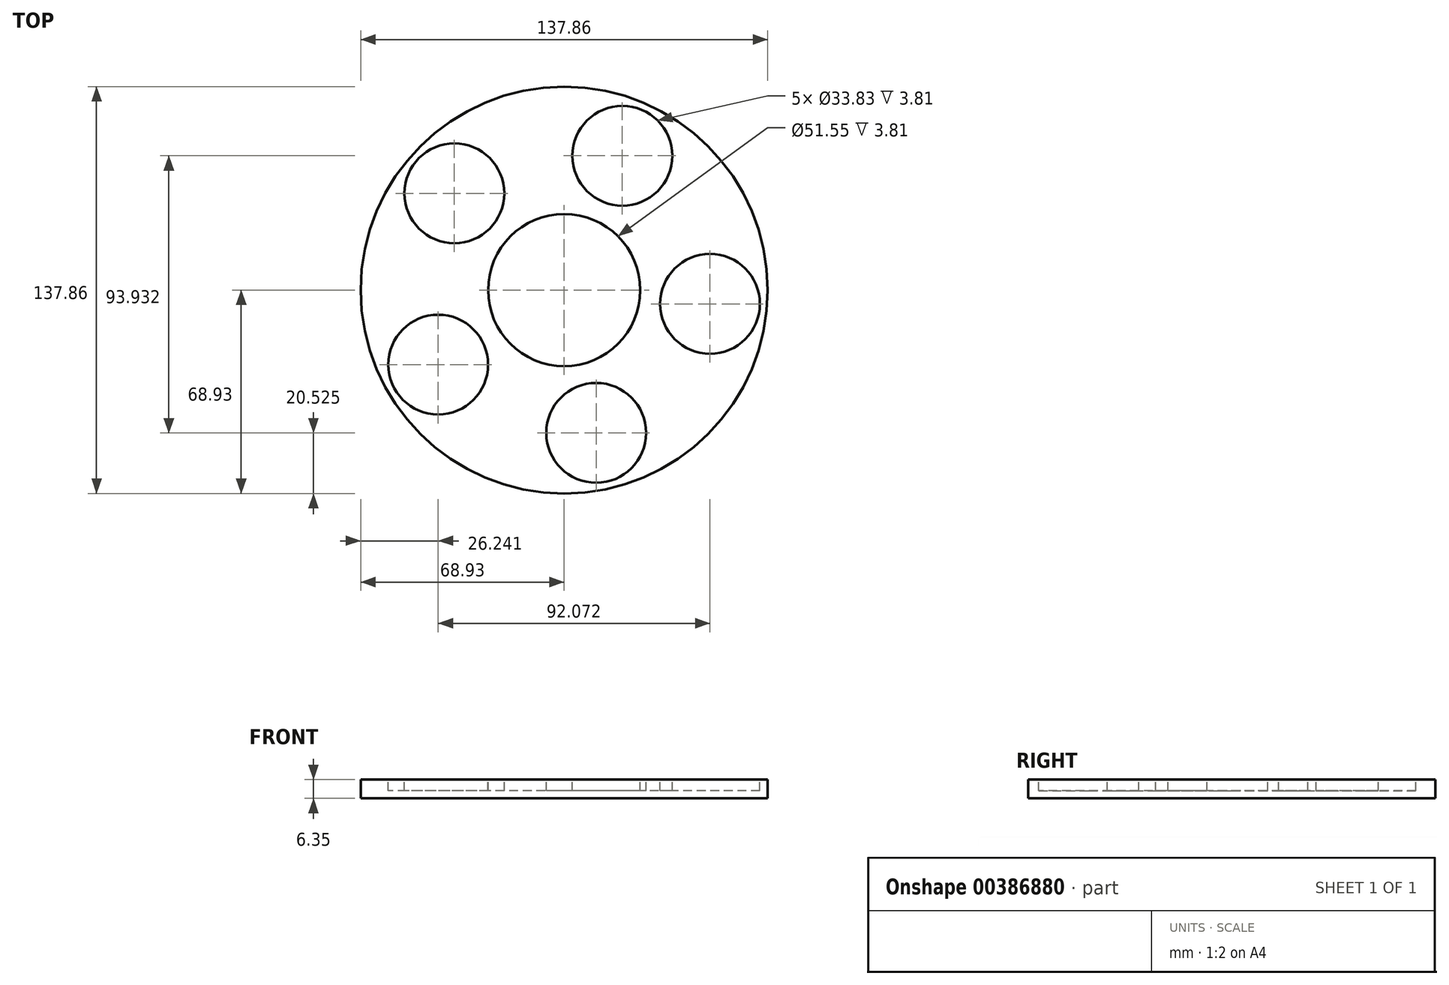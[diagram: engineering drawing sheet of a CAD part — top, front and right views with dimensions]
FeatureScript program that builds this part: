
annotation { "Feature Type Name" : "Feature", "Feature Type Description" : "" }
export const myFeature = defineFeature(function(context is Context, id is Id, definition is map)
    precondition{}
    {
        {
            var Q0;
            Q0=qCreatedBy(makeId("Top.planeOp"),FACE);
            var sketch = newSketch(context, id + "F0", { "sketchPlane" : qUnion([Q0])});
            skCircle(sketch, "E0", {"center": v(0, 0) * mm, "radius": 68.93 * mm});
            skSolve(sketch);
        }
        {
            var Q0;
            Q0 = qSketchRegion(id + "F0", true);
            var Q1;
            Q1 = qSketchRegion(id + "F2", true);
            extrude(context, id + "F1", {"entities" : qUnion([Q0, Q1]), "depth" : 6.35 * mm});
        }
        {
            var Q0;
            Q0=makeQuery(id+"F1.opExtrude","CAP_FACE",FACE,{"disambiguationData":[OSD([sQuery(id+"F0.wireOp",EDGE,"E0")])],"isStart":false});
            var sketch = newSketch(context, id + "F2", { "sketchPlane" : qUnion([Q0])});
            skCircle(sketch, "E1", {"center": v(0, 0) * mm, "radius": 25.78 * mm});
            skSolve(sketch);
        }
        {
            var Q0;
            Q0=makeQuery(id+"F2.imprint","IMPRINT",FACE,{"disambiguationData":[TD([[makeQuery(id+"F2.imprint","IMPRINT",EDGE,{"derivedFrom":sQuery(id+"F2.wireOp",EDGE,"E1")}),1.0]])]});
            extrude(context, id + "F3", {"entities" : qUnion([Q0]), "operationType" : NewBodyOperationType.REMOVE, "oppositeDirection" : true, "depth" : 3.8 * mm});
        }
        {
            var Q0;
            Q0=makeQuery(id+"F1.opExtrude","CAP_FACE",FACE,{"disambiguationData":[OSD([sQuery(id+"F0.wireOp",EDGE,"E0")])],"isStart":false});
            var sketch = newSketch(context, id + "F4", { "sketchPlane" : qUnion([Q0])});
            skSolve(sketch);
        }
        {
            var Q0;
            Q0=makeQuery(id+"F4.imprint","IMPRINT",FACE,{"disambiguationData":[TD([[makeQuery(id+"F4.imprint","IMPRINT",EDGE,{"derivedFrom":makeQuery(id+"F1.opExtrude","CAP_EDGE",EDGE,{"disambiguationData":[OSD([sQuery(id+"F0.wireOp",EDGE,"E0")])],"isStart":false})}),1.0]])]});
            var sketch = newSketch(context, id + "F5", { "sketchPlane" : qUnion([Q0])});
            skCircle(sketch, "E2", {"center": v(-37.21, 32.8) * mm, "radius": 16.91 * mm});
            skCircle(sketch, "E3.1.0", {"center": v(-42.69, -25.26) * mm, "radius": 16.91 * mm});
            skCircle(sketch, "E3.2.0", {"center": v(10.83, -48.4) * mm, "radius": 16.91 * mm});
            skCircle(sketch, "E3.3.0", {"center": v(49.38, -4.66) * mm, "radius": 16.91 * mm});
            skCircle(sketch, "E3.4.0", {"center": v(19.69, 45.53) * mm, "radius": 16.91 * mm});
            skPoint(sketch, "E3.center", {"position": v(0, 0) * mm});
            skSolve(sketch);
        }
        {
            var Q0;
            Q0=makeQuery(id+"F5.imprint","IMPRINT",FACE,{"disambiguationData":[TD([[makeQuery(id+"F5.imprint","IMPRINT",EDGE,{"derivedFrom":sQuery(id+"F5.wireOp",EDGE,"E3.1.0")}),1.0]])]});
            var Q1;
            Q1=makeQuery(id+"F5.imprint","IMPRINT",FACE,{"disambiguationData":[TD([[makeQuery(id+"F5.imprint","IMPRINT",EDGE,{"derivedFrom":sQuery(id+"F5.wireOp",EDGE,"E2")}),1.0]])]});
            var Q2;
            Q2=makeQuery(id+"F5.imprint","IMPRINT",FACE,{"disambiguationData":[TD([[makeQuery(id+"F5.imprint","IMPRINT",EDGE,{"derivedFrom":sQuery(id+"F5.wireOp",EDGE,"E3.4.0")}),1.0]])]});
            var Q3;
            Q3=makeQuery(id+"F5.imprint","IMPRINT",FACE,{"disambiguationData":[TD([[makeQuery(id+"F5.imprint","IMPRINT",EDGE,{"derivedFrom":sQuery(id+"F5.wireOp",EDGE,"E3.3.0")}),1.0]])]});
            var Q4;
            Q4=makeQuery(id+"F5.imprint","IMPRINT",FACE,{"disambiguationData":[TD([[makeQuery(id+"F5.imprint","IMPRINT",EDGE,{"derivedFrom":sQuery(id+"F5.wireOp",EDGE,"E3.2.0")}),1.0]])]});
            extrude(context, id + "F6", {"entities" : qUnion([Q0, Q1, Q2, Q3, Q4]), "operationType" : NewBodyOperationType.REMOVE, "oppositeDirection" : true, "depth" : 3.8 * mm});
        }
    });
